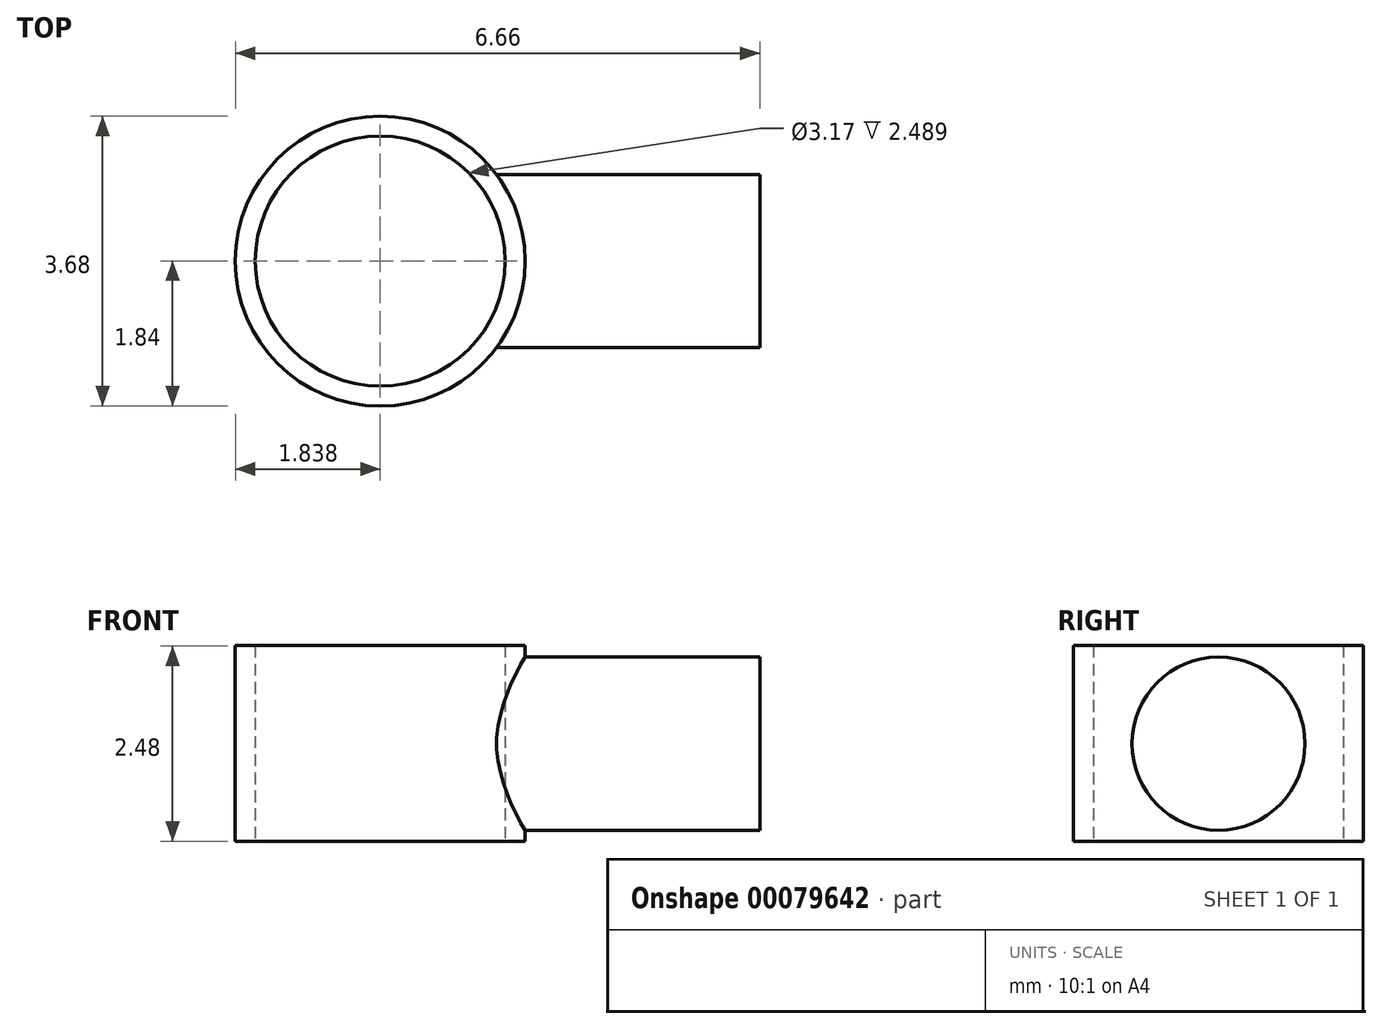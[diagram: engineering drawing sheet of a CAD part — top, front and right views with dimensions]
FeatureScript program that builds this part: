
annotation { "Feature Type Name" : "Feature", "Feature Type Description" : "" }
export const myFeature = defineFeature(function(context is Context, id is Id, definition is map)
    precondition{}
    {
        {
            var Q0;
            Q0=qCreatedBy(makeId("Top.planeOp"),FACE);
            var sketch = newSketch(context, id + "F0", { "sketchPlane" : qUnion([Q0])});
            skLineSegment(sketch, "E0.bottom", {"start": v(-5.04, 4) * mm, "end": v(5.04, 4) * mm});
            skLineSegment(sketch, "E0.top", {"start": v(-5.04, -4) * mm, "end": v(5.04, -4) * mm});
            skLineSegment(sketch, "E0.left", {"start": v(-5.04, 4) * mm, "end": v(-5.04, -4) * mm});
            skLineSegment(sketch, "E0.right", {"start": v(5.04, 4) * mm, "end": v(5.04, -4) * mm});
            skCircle(sketch, "E1", {"center": v(-0.68, 0) * mm, "radius": 1.59 * mm});
            skLineSegment(sketch, "E2", {"start": v(0.9, 0) * mm, "end": v(5.04, 0) * mm});
            skCircle(sketch, "E3", {"center": v(-0.68, 0) * mm, "radius": 1.84 * mm});
            skSolve(sketch);
        }
        {
            var Q0;
            Q0=makeQuery(id+"F0.imprint","IMPRINT",FACE,{"disambiguationData":[TD([[makeQuery(id+"F0.imprint","IMPRINT",EDGE,{"derivedFrom":sQuery(id+"F0.wireOp",EDGE,"E1")}),-1.0]])]});
            extrude(context, id + "F1", {"entities" : qUnion([Q0]), "endBound" : BoundingType.SYMMETRIC, "depth" : 2.5 * mm});
        }
        {
            var Q0;
            Q0=qCreatedBy(makeId("Right.planeOp"),FACE);
            var sketch = newSketch(context, id + "F2", { "sketchPlane" : qUnion([Q0])});
            skCircle(sketch, "E4", {"center": v(0, 0) * mm, "radius": 1.1 * mm});
            skSolve(sketch);
        }
        {
            var Q0;
            Q0 = qSketchRegion(id + "F2", true);
            extrude(context, id + "F3", {"entities" : qUnion([Q0]), "operationType" : NewBodyOperationType.ADD, "depth" : 4.14 * mm});
        }
        {
            var Q0;
            Q0=makeQuery(id+"F0.imprint","IMPRINT",FACE,{"disambiguationData":[TD([[makeQuery(id+"F0.imprint","IMPRINT",EDGE,{"derivedFrom":sQuery(id+"F0.wireOp",EDGE,"E1")}),1.0]])]});
            extrude(context, id + "F4", {"entities" : qUnion([Q0]), "operationType" : NewBodyOperationType.REMOVE, "endBound" : BoundingType.SYMMETRIC, "oppositeDirection" : true, "depth" : 25.4 * mm});
        }
    });
